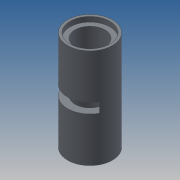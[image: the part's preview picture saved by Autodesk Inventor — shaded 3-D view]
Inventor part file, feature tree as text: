
AUTODESK INVENTOR PART (.ipt)
format: ipt  version: 2022.2 (Build 262287000, 287)  size: 133,120 bytes
history: native  units: in
note: dims shown in document units (in); Inventor stores cm internally (conversion verified against a paired STEP export)
features: sketch x2, revolve x1, extrude x1
ambient origin geometry x8: Origin, YZ Plane, XZ Plane, XY Plane, X Axis, Y Axis, Z Axis, Center Point
bodies: Solid1 (feature_tree)
feature tree (4):
  revolve  "Revolution1"  [1 undecoded]
  extrude  "Extrusion1"  Depth=0.3937in
  sketch  "Sketch2"  dims[d0=0.6299in d1=0.252in]
  sketch  "Sketch3"  dims[d2=0.2835in d3=0.189in d4=0.0315in d5=0.063in d6=90.0deg d7=0.3937in d8=0.0in]
note: 1 required parameter value undecoded (feature->parameter linkage not recoverable at this tier; creation-order binding heuristic only, values carry confidence <= 0.55)
